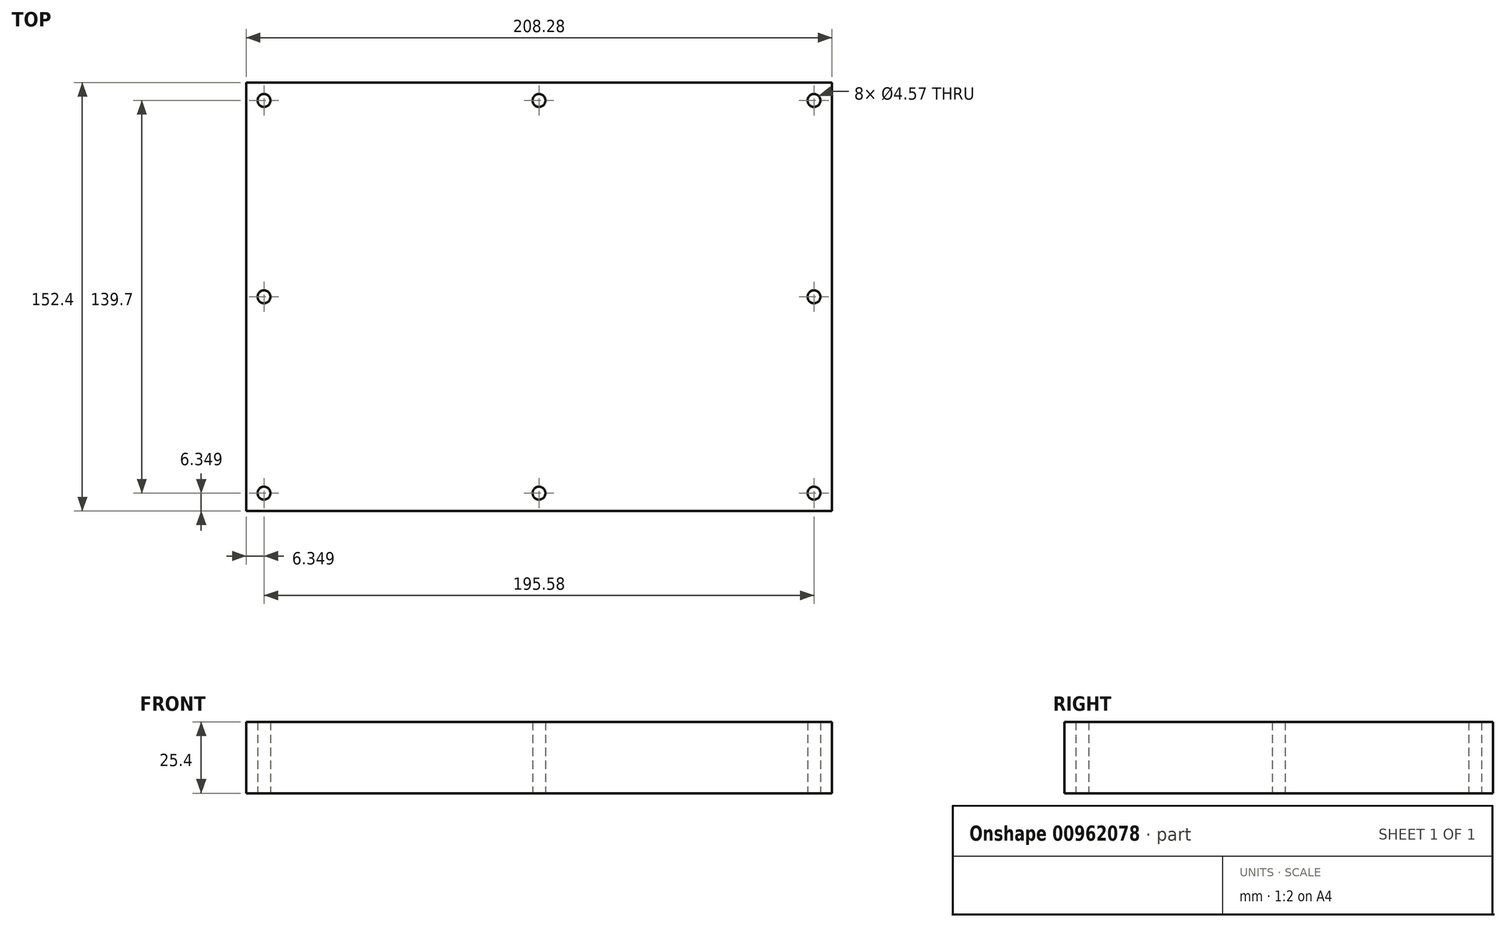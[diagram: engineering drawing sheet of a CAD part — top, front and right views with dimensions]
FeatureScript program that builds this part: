
annotation { "Feature Type Name" : "Feature", "Feature Type Description" : "" }
export const myFeature = defineFeature(function(context is Context, id is Id, definition is map)
    precondition{}
    {
        {
            var Q0;
            Q0=qCreatedBy(makeId("Top.planeOp"),FACE);
            var sketch = newSketch(context, id + "F0", { "sketchPlane" : qUnion([Q0])});
            skLineSegment(sketch, "E0.bottom", {"start": v(-99.56, 76.95) * mm, "end": v(108.72, 76.95) * mm});
            skLineSegment(sketch, "E0.top", {"start": v(-99.56, -75.45) * mm, "end": v(108.72, -75.45) * mm});
            skLineSegment(sketch, "E0.left", {"start": v(-99.56, 76.95) * mm, "end": v(-99.56, -75.45) * mm});
            skLineSegment(sketch, "E0.right", {"start": v(108.72, 76.95) * mm, "end": v(108.72, -75.45) * mm});
            skLineSegment(sketch, "E1.bottom", {"start": v(-86.86, 64.25) * mm, "end": v(96.02, 64.25) * mm});
            skLineSegment(sketch, "E1.top", {"start": v(-86.86, -62.75) * mm, "end": v(96.02, -62.75) * mm});
            skLineSegment(sketch, "E1.left", {"start": v(-86.86, 64.25) * mm, "end": v(-86.86, -62.75) * mm});
            skLineSegment(sketch, "E1.right", {"start": v(96.02, 64.25) * mm, "end": v(96.02, -62.75) * mm});
            skLineSegment(sketch, "E2", {"start": v(96.02, 64.25) * mm, "end": v(108.72, 64.25) * mm, "construction": true});
            skLineSegment(sketch, "E3", {"start": v(-86.86, -62.75) * mm, "end": v(-86.86, -75.45) * mm, "construction": true});
            skLineSegment(sketch, "E4", {"start": v(-86.86, -69.1) * mm, "end": v(-99.56, -69.1) * mm});
            skLineSegment(sketch, "E5", {"start": v(-99.56, -69.1) * mm, "end": v(108.72, -69.1) * mm, "construction": true});
            skLineSegment(sketch, "E6", {"start": v(-93.21, -69.1) * mm, "end": v(-93.21, 76.95) * mm, "construction": true});
            skLineSegment(sketch, "E7", {"start": v(41.22, 64.25) * mm, "end": v(41.22, 76.95) * mm, "construction": true});
            skLineSegment(sketch, "E8", {"start": v(-93.21, 70.6) * mm, "end": v(108.72, 70.6) * mm, "construction": true});
            skLineSegment(sketch, "E9", {"start": v(96.02, 0.75) * mm, "end": v(108.72, 0.75) * mm, "construction": true});
            skLineSegment(sketch, "E10", {"start": v(102.37, 0.75) * mm, "end": v(102.37, 70.6) * mm, "construction": true});
            skLineSegment(sketch, "E11", {"start": v(102.37, 0.75) * mm, "end": v(102.37, -69.1) * mm, "construction": true});
            skLineSegment(sketch, "E12", {"start": v(96.02, -62.75) * mm, "end": v(108.72, -62.75) * mm});
            skLineSegment(sketch, "E13", {"start": v(96.02, -62.75) * mm, "end": v(96.02, -75.45) * mm});
            skLineSegment(sketch, "E14", {"start": v(96.01, 76.95) * mm, "end": v(96.02, 64.25) * mm});
            skLineSegment(sketch, "E15", {"start": v(-86.91, -62.76) * mm, "end": v(-86.86, -75.45) * mm});
            skLineSegment(sketch, "E16", {"start": v(-86.86, -62.75) * mm, "end": v(-99.56, -62.75) * mm});
            skLineSegment(sketch, "E17", {"start": v(-86.86, 64.25) * mm, "end": v(-86.86, 76.95) * mm});
            skLineSegment(sketch, "E18", {"start": v(-86.86, 64.25) * mm, "end": v(-99.56, 64.25) * mm});
            skLineSegment(sketch, "E19", {"start": v(4.58, 76.95) * mm, "end": v(4.58, -75.45) * mm, "construction": true});
            skCircle(sketch, "E20", {"center": v(-93.21, -69.1) * mm, "radius": 2.29 * mm});
            skCircle(sketch, "E21", {"center": v(102.37, 70.6) * mm, "radius": 2.29 * mm});
            skCircle(sketch, "E22", {"center": v(102.37, 0.75) * mm, "radius": 2.29 * mm});
            skCircle(sketch, "E23", {"center": v(102.37, -69.1) * mm, "radius": 2.29 * mm});
            skCircle(sketch, "E24", {"center": v(4.58, -69.1) * mm, "radius": 2.29 * mm});
            skCircle(sketch, "E25", {"center": v(-93.21, 70.6) * mm, "radius": 2.29 * mm});
            skCircle(sketch, "E26", {"center": v(4.58, 70.6) * mm, "radius": 2.29 * mm});
            skCircle(sketch, "E27", {"center": v(-93.21, 0.75) * mm, "radius": 2.29 * mm});
            skPoint(sketch, "E27.perimeterSnap0", {"position": v(-86.86, 0.75) * mm});
            skPoint(sketch, "E27.perimeterSnap1", {"position": v(-93.21, 3.92) * mm});
            skSolve(sketch);
        }
        {
            var Q0;
            Q0=makeQuery(id+"F0.imprint","IMPRINT",FACE,{"disambiguationData":[TD([[makeQuery(id+"F0.imprint","IMPRINT",EDGE,{"derivedFrom":sQuery(id+"F0.wireOp",EDGE,"E1.left")}),-1.0]])]});
            var Q1;
            Q1=makeQuery(id+"F0.imprint","IMPRINT",FACE,{"disambiguationData":[TD([[makeQuery(id+"F0.imprint","IMPRINT",EDGE,{"derivedFrom":sQuery(id+"F0.wireOp",EDGE,"E1.bottom")}),1.0]])]});
            var Q2;
            Q2=makeQuery(id+"F0.imprint","IMPRINT",FACE,{"disambiguationData":[TD([[makeQuery(id+"F0.imprint","IMPRINT",EDGE,{"derivedFrom":sQuery(id+"F0.wireOp",EDGE,"E1.right")}),1.0]])]});
            var Q3;
            Q3=makeQuery(id+"F0.imprint","IMPRINT",FACE,{"disambiguationData":[TD([[makeQuery(id+"F0.imprint","IMPRINT",EDGE,{"derivedFrom":sQuery(id+"F0.wireOp",EDGE,"E1.bottom")}),-1.0]])]});
            var Q4;
            {var subQ6=sQuery(id+"F0.wireOp",EDGE,"E0.left");var subQ7=sQuery(id+"F0.wireOp",EDGE,"E0.top");var subQ8=makeQuery(id+"F0.imprint","INTERSECT",VERTEX,{"derivedFrom":[subQ7,subQ6]});Q4=makeQuery(id+"F0.imprint","IMPRINT",FACE,{"disambiguationData":[TD([[makeQuery(id+"F0.imprint","IMPRINT",EDGE,{"disambiguationData":[TD([[subQ8,-1.0]])],"derivedFrom":subQ7}),1.0]])]});}
            var Q5;
            Q5=makeQuery(id+"F0.imprint","IMPRINT",FACE,{"disambiguationData":[TD([[makeQuery(id+"F0.imprint","IMPRINT",EDGE,{"derivedFrom":sQuery(id+"F0.wireOp",EDGE,"E1.top")}),-1.0]])]});
            var Q6;
            {var subQ0=sQuery(id+"F0.wireOp",EDGE,"E17");Q6=makeQuery(id+"F0.imprint","IMPRINT",FACE,{"disambiguationData":[TD([[makeQuery(id+"F0.imprint","IMPRINT",EDGE,{"derivedFrom":subQ0}),1.0]])]});}
            var Q7;
            {var subQ0=sQuery(id+"F0.wireOp",EDGE,"E12");Q7=makeQuery(id+"F0.imprint","IMPRINT",FACE,{"disambiguationData":[TD([[makeQuery(id+"F0.imprint","IMPRINT",EDGE,{"derivedFrom":subQ0}),-1.0]])]});}
            extrude(context, id + "F1", {"entities" : qUnion([Q0, Q1, Q2, Q3, Q4, Q5, Q6, Q7]), "depth" : 25.4 * mm, "offsetDistance" : 25.4 * mm});
        }
    });
